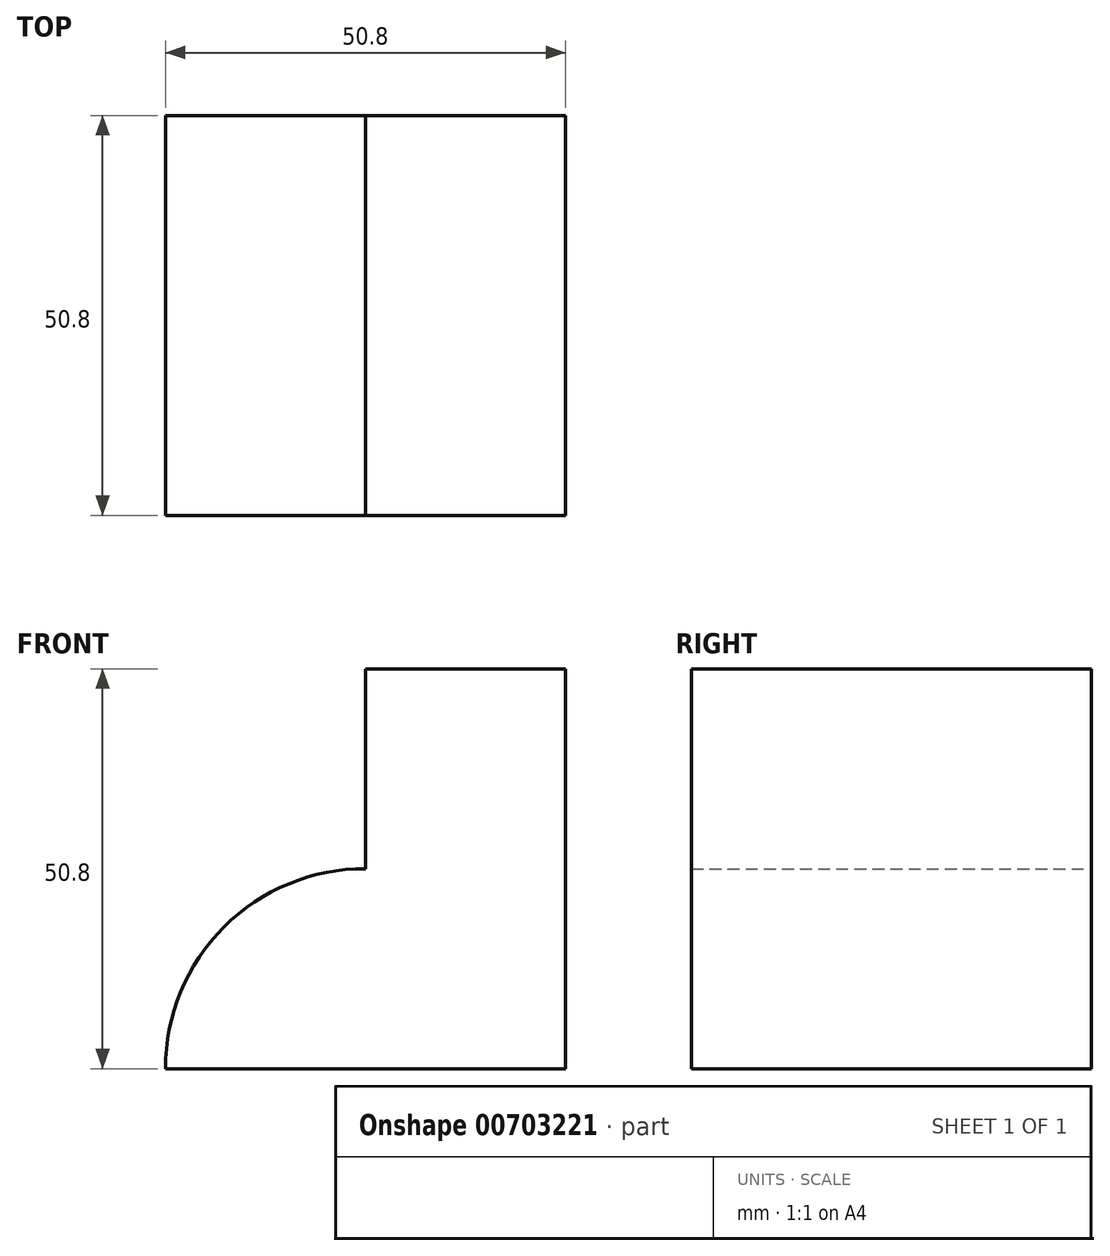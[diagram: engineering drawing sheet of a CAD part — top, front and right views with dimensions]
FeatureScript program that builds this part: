
annotation { "Feature Type Name" : "Feature", "Feature Type Description" : "" }
export const myFeature = defineFeature(function(context is Context, id is Id, definition is map)
    precondition{}
    {
        {
            var Q0;
            Q0=qCreatedBy(makeId("Front.planeOp"),FACE);
            var sketch = newSketch(context, id + "F0", { "sketchPlane" : qUnion([Q0])});
            skLineSegment(sketch, "E0", {"start": v(-28.55, -20.9) * mm, "end": v(22.25, -20.9) * mm});
            skLineSegment(sketch, "E1", {"start": v(22.25, -20.9) * mm, "end": v(22.25, 29.9) * mm});
            skLineSegment(sketch, "E2", {"start": v(22.25, 29.9) * mm, "end": v(-3.15, 29.9) * mm});
            skLineSegment(sketch, "E3", {"start": v(-3.15, 29.9) * mm, "end": v(-3.15, 4.5) * mm});
            skArc(sketch, "E4", {"start": v(-3.15, 4.5) * mm, "mid": v(-21.14, -2.91) * mm, "end": v(-28.55, -20.9) * mm});
            skSolve(sketch);
        }
        {
            var Q0;
            Q0 = qSketchRegion(id + "F0", true);
            extrude(context, id + "F1", {"entities" : qUnion([Q0]), "depth" : 50.8 * mm, "offsetDistance" : 25.4 * mm});
        }
    });
